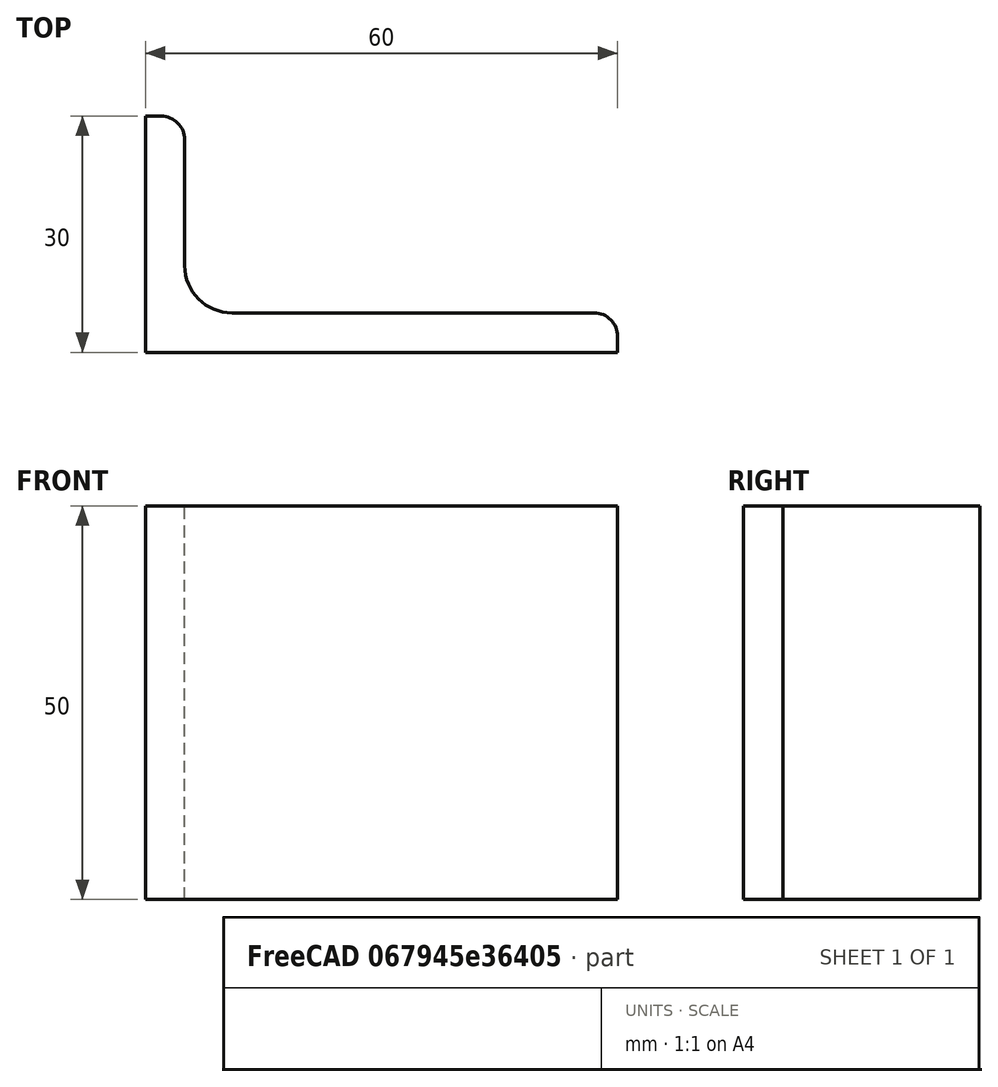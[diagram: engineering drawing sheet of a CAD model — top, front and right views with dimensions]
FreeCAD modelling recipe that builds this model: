
FCSTD DOCUMENT  (FreeCAD 0.15R4671 (Git))
Label: Angle Bar 60x30x5 EN10056 S235JR
License: All rights reserved
LicenseURL: http://en.wikipedia.org/wiki/All_rights_reserved
objects: Sketcher::SketchObject×1, Part::Extrusion×1
note: 2 computed .brp shape members not serialized (recipe doc carries the construction recipe); baked Part::Feature solids carry a one-line shape summary decoded from their .brp

FEATURE [Sketcher::SketchObject] Sketch
  sketch-geometry (9):
    g0: LineSegment StartX=0 StartY=0 StartZ=0 EndX=60 EndY=0 EndZ=0
    g1: LineSegment StartX=60 StartY=0 StartZ=0 EndX=60 EndY=2 EndZ=0
    g2: LineSegment StartX=57 StartY=5 StartZ=0 EndX=11 EndY=5 EndZ=0
    g3: LineSegment StartX=0 StartY=0 StartZ=0 EndX=0 EndY=30 EndZ=0
    g4: LineSegment StartX=0 StartY=30 StartZ=0 EndX=2 EndY=30 EndZ=0
    g5: LineSegment StartX=5 StartY=27 StartZ=0 EndX=5 EndY=11 EndZ=0
    g6: ArcOfCircle CenterX=11 CenterY=11 CenterZ=0 NormalX=0 NormalY=0 NormalZ=1 Radius=6 StartAngle=3.14159 EndAngle=4.71239
    g7: ArcOfCircle CenterX=2 CenterY=27 CenterZ=0 NormalX=0 NormalY=0 NormalZ=1 Radius=3 StartAngle=0 EndAngle=1.5708
    g8: ArcOfCircle CenterX=57 CenterY=2 CenterZ=0 NormalX=0 NormalY=0 NormalZ=1 Radius=3 StartAngle=0 EndAngle=1.5708
  constraints (23):
    c: Coincident(g0,g-1)
    c: Horizontal(g0)
    c: Coincident(g1,g0)
    c: Vertical(g1)
    c: Horizontal(g2)
    c: Coincident(g3,g-1)
    c: Vertical(g3)
    c: Coincident(g4,g3)
    c: Horizontal(g4)
    c: Vertical(g5)
    c: Tangent(g5,g6) = -1.5708
    c: Tangent(g2,g6) = 1.5708
    c: Tangent(g4,g7) = 1.5708
    c: Tangent(g5,g7) = 1.5708
    c: Tangent(g2,g8) = -1.5708
    c: Tangent(g1,g8) = -1.5708
    c: DistanceX(g0) = 60
    c: DistanceY(g3) = 30
    c: DistanceY(g0,g2) = 5
    c: DistanceX(g3,g5) = 5
    c: Radius(g6) = 6
    c: Radius(g8) = 3
    c: Radius(g7) = 3
FEATURE [Part::Extrusion] Extrude  label="Angle Bar 60x30x5 EN10056 S235JR"
  Base = -> Sketch
  Dir = (0,0,50)
  Solid = true
